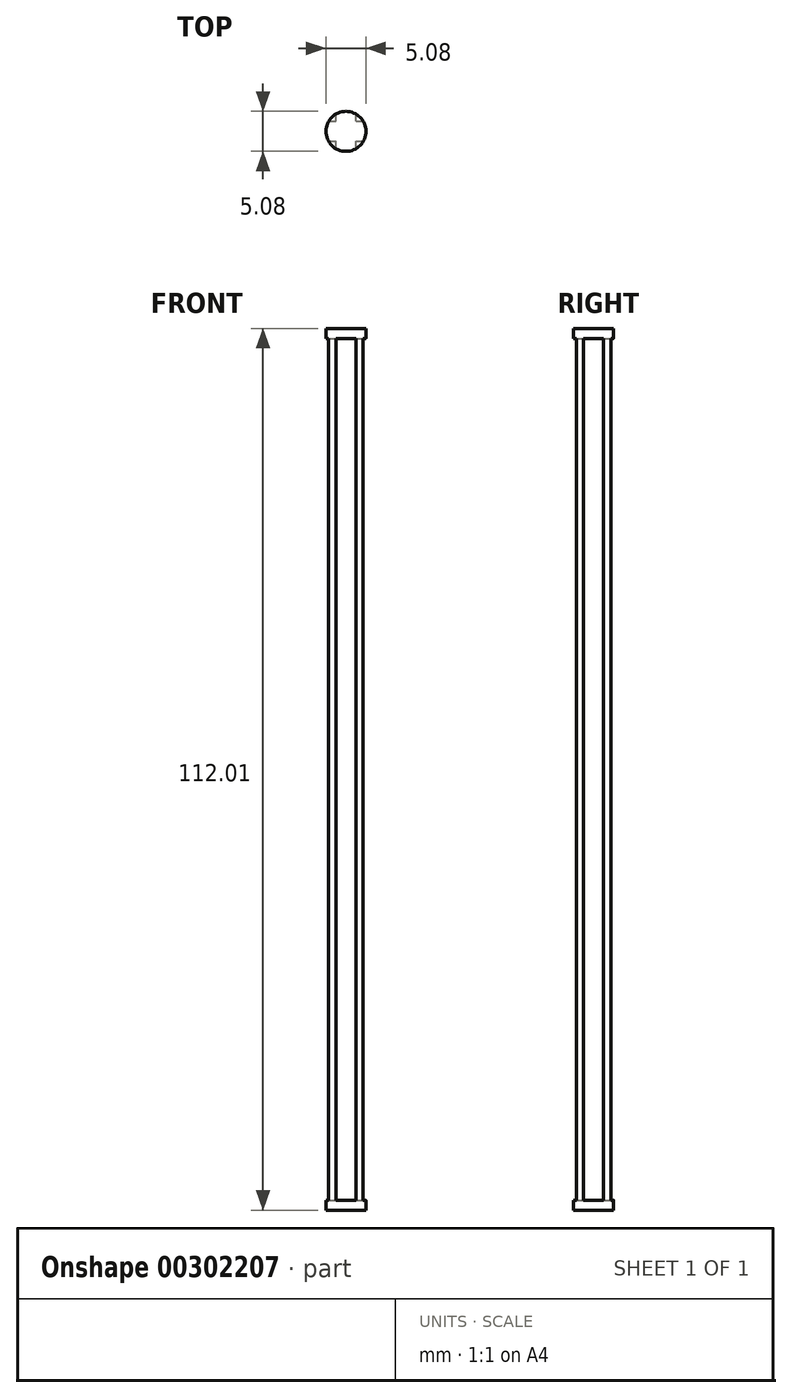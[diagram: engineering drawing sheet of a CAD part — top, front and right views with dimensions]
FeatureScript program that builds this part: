
annotation { "Feature Type Name" : "Feature", "Feature Type Description" : "" }
export const myFeature = defineFeature(function(context is Context, id is Id, definition is map)
    precondition{}
    {
        {
            var Q0;
            Q0=qCreatedBy(makeId("Top.planeOp"),FACE);
            var sketch = newSketch(context, id + "F0", { "sketchPlane" : qUnion([Q0])});
            skLineSegment(sketch, "E0", {"start": v(-4.58, -5.63) * mm, "end": v(0.5, -5.63) * mm});
            skLineSegment(sketch, "E1", {"start": v(-4.58, -5.63) * mm, "end": v(-4.58, -0.55) * mm});
            skLineSegment(sketch, "E2", {"start": v(-4.58, -0.55) * mm, "end": v(0.5, -0.55) * mm});
            skLineSegment(sketch, "E3", {"start": v(0.5, -0.55) * mm, "end": v(0.5, -5.63) * mm});
            skSolve(sketch);
        }
        {
            var Q0;
            Q0 = qSketchRegion(id + "F0", true);
            extrude(context, id + "F1", {"entities" : qUnion([Q0]), "depth" : 36.83 * mm, "hasSecondDirection" : true, "secondDirectionOppositeDirection" : true, "secondDirectionDepth" : 75.18 * mm});
        }
        {
            var Q0;
            Q0=qCreatedBy(makeId("Front.planeOp"),FACE);
            var sketch = newSketch(context, id + "F2", { "sketchPlane" : qUnion([Q0])});
            skLineSegment(sketch, "E4", {"start": v(-3.3, 35.56) * mm, "end": v(-0.77, 35.56) * mm});
            skLineSegment(sketch, "E5", {"start": v(-0.77, 35.56) * mm, "end": v(-0.77, -73.91) * mm});
            skLineSegment(sketch, "E6", {"start": v(-0.77, -73.91) * mm, "end": v(-3.3, -73.91) * mm});
            skLineSegment(sketch, "E7", {"start": v(-3.3, -73.91) * mm, "end": v(-3.3, 35.56) * mm});
            skSolve(sketch);
        }
        {
            var Q0;
            Q0 = qSketchRegion(id + "F2", true);
            extrude(context, id + "F3", {"entities" : qUnion([Q0]), "operationType" : NewBodyOperationType.REMOVE, "depth" : 23.1 * mm});
        }
        {
            var Q0;
            Q0=qCreatedBy(makeId("Right.planeOp"),FACE);
            var sketch = newSketch(context, id + "F4", { "sketchPlane" : qUnion([Q0])});
            skLineSegment(sketch, "E8", {"start": v(-1.82, 35.56) * mm, "end": v(-4.36, 35.56) * mm});
            skLineSegment(sketch, "E9", {"start": v(-4.36, 35.56) * mm, "end": v(-4.36, -73.91) * mm});
            skLineSegment(sketch, "E10", {"start": v(-4.36, -73.91) * mm, "end": v(-1.82, -73.91) * mm});
            skLineSegment(sketch, "E11", {"start": v(-1.82, -73.91) * mm, "end": v(-1.82, 35.56) * mm});
            skSolve(sketch);
        }
        {
            var Q0;
            Q0 = qSketchRegion(id + "F4", true);
            extrude(context, id + "F5", {"entities" : qUnion([Q0]), "operationType" : NewBodyOperationType.REMOVE, "endBound" : BoundingType.THROUGH_ALL, "oppositeDirection" : true, "depth" : 25.4 * mm, "hasSecondDirection" : true, "secondDirectionOppositeDirection" : false, "secondDirectionDepth" : 29.97 * mm});
        }
        {
            var Q0;
            Q0=makeQuery(id+"F1.opExtrude","SWEPT_EDGE",EDGE,{"disambiguationData":[OSD([sQuery(id+"F0.wireOp",EDGE,"E0"),sQuery(id+"F0.wireOp",EDGE,"E3")])]});
            var Q1;
            Q1=makeQuery(id+"F1.opExtrude","SWEPT_EDGE",EDGE,{"disambiguationData":[OSD([sQuery(id+"F0.wireOp",EDGE,"E0"),sQuery(id+"F0.wireOp",EDGE,"E1")])]});
            var Q2;
            Q2=makeQuery(id+"F1.opExtrude","SWEPT_EDGE",EDGE,{"disambiguationData":[OSD([sQuery(id+"F0.wireOp",EDGE,"E1"),sQuery(id+"F0.wireOp",EDGE,"E2")])]});
            var Q3;
            Q3=makeQuery(id+"F1.opExtrude","SWEPT_EDGE",EDGE,{"disambiguationData":[OSD([sQuery(id+"F0.wireOp",EDGE,"E2"),sQuery(id+"F0.wireOp",EDGE,"E3")])]});
            fillet(context, id + "F6", {"entities" : qUnion([Q0, Q1, Q2, Q3]), "radius" : 2.54 * mm, "tangentPropagation" : true, "allowEdgeOverflow" : false});
        }
    });
